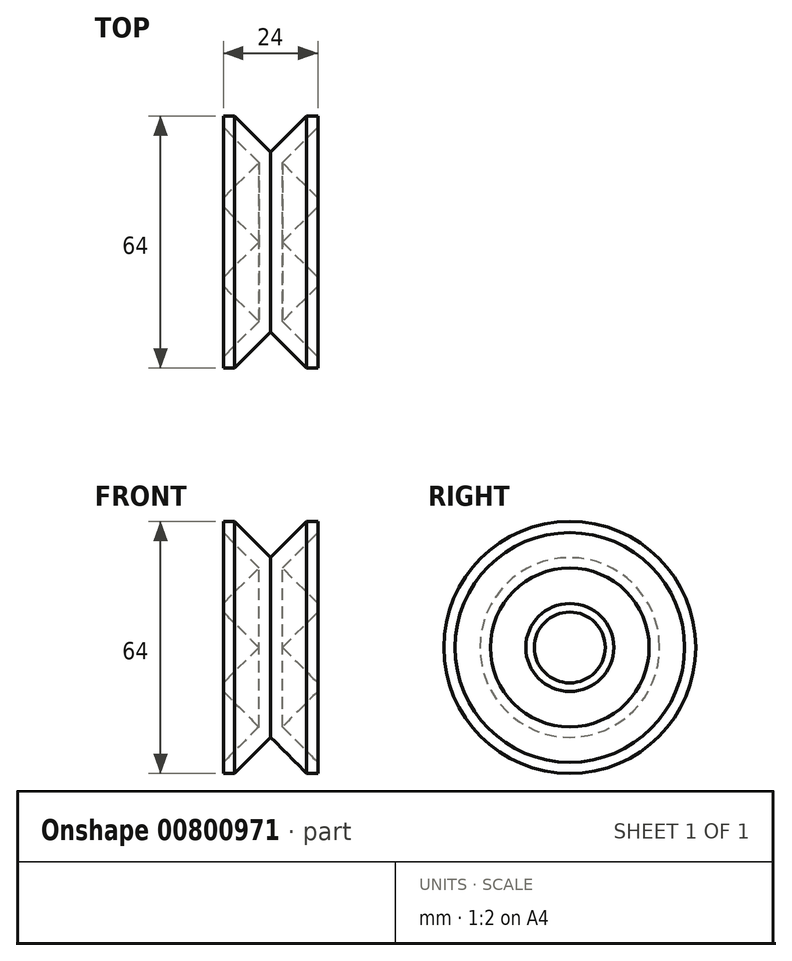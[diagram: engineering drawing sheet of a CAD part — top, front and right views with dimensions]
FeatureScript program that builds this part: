
annotation { "Feature Type Name" : "Feature", "Feature Type Description" : "" }
export const myFeature = defineFeature(function(context is Context, id is Id, definition is map)
    precondition{}
    {
        {
            var Q0;
            Q0=qCreatedBy(makeId("Top.planeOp"),FACE);
            var sketch = newSketch(context, id + "F0", { "sketchPlane" : qUnion([Q0])});
            skLineSegment(sketch, "E0", {"start": v(9, 0) * mm, "end": v(0, -9) * mm});
            skLineSegment(sketch, "E1", {"start": v(0, -9) * mm, "end": v(0, -11.17) * mm});
            skLineSegment(sketch, "E2", {"start": v(0, -11.17) * mm, "end": v(9, -20.17) * mm});
            skLineSegment(sketch, "E3", {"start": v(9, -20.17) * mm, "end": v(0, -29.17) * mm});
            skLineSegment(sketch, "E4", {"start": v(0, -29.17) * mm, "end": v(0, -32) * mm});
            skLineSegment(sketch, "E5", {"start": v(0, -32) * mm, "end": v(2.83, -32) * mm});
            skLineSegment(sketch, "E6", {"start": v(2.83, -32) * mm, "end": v(12, -22.83) * mm});
            skLineSegment(sketch, "E7", {"start": v(12, -22.83) * mm, "end": v(21.17, -32) * mm});
            skPoint(sketch, "E7.endSnap0", {"position": v(1.41, -32) * mm});
            skLineSegment(sketch, "E8", {"start": v(21.17, -32) * mm, "end": v(24, -32) * mm});
            skLineSegment(sketch, "E9", {"start": v(24, -32) * mm, "end": v(24, -29.17) * mm});
            skLineSegment(sketch, "E10", {"start": v(24, -29.17) * mm, "end": v(15, -20.17) * mm});
            skLineSegment(sketch, "E11", {"start": v(15, -20.17) * mm, "end": v(24, -11.17) * mm});
            skLineSegment(sketch, "E12", {"start": v(24, -11.17) * mm, "end": v(24, -9) * mm});
            skLineSegment(sketch, "E13", {"start": v(24, -9) * mm, "end": v(15, 0) * mm});
            skLineSegment(sketch, "E14", {"start": v(15, 0) * mm, "end": v(9, 0) * mm});
            skLineSegment(sketch, "E15", {"start": v(0, -9) * mm, "end": v(24, -9) * mm, "construction": true});
            skLineSegment(sketch, "E16", {"start": v(9, -20.17) * mm, "end": v(9, 0) * mm, "construction": true});
            skLineSegment(sketch, "E17", {"start": v(12, -17.51) * mm, "end": v(4.57, -10.09) * mm});
            skLineSegment(sketch, "E18", {"start": v(4.57, -10.09) * mm, "end": v(12, -2.66) * mm});
            skLineSegment(sketch, "E19", {"start": v(12, -2.66) * mm, "end": v(19.43, -10.09) * mm});
            skLineSegment(sketch, "E20", {"start": v(19.43, -10.09) * mm, "end": v(12, -17.51) * mm});
            skSolve(sketch);
        }
        {
            var Q0;
            Q0=makeQuery(id+"F0.imprint","IMPRINT",FACE,{"disambiguationData":[TD([[makeQuery(id+"F0.imprint","IMPRINT",EDGE,{"derivedFrom":sQuery(id+"F0.wireOp",EDGE,"E0")}),1.0]])]});
            var Q1;
            Q1=makeQuery(id+"F0.imprint","IMPRINT",FACE,{"disambiguationData":[TD([[makeQuery(id+"F0.imprint","IMPRINT",EDGE,{"derivedFrom":sQuery(id+"F0.wireOp",EDGE,"E17")}),-1.0]])]});
            var Q2;
            Q2=sQuery(id+"F0.wireOp",EDGE,"E14");
            revolve(context, id + "F1", {"surfaceOperationType" : NewSurfaceOperationType.NEW, "entities" : qUnion([Q0, Q1]), "axis" : qUnion([Q2]), "revolveType" : RevolveType.FULL});
        }
    });
